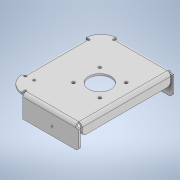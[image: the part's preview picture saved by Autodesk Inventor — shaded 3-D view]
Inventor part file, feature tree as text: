
AUTODESK INVENTOR PART (.ipt)
format: ipt  version: 2021 (Build 250183000, 183)  size: 284,160 bytes
history: native  units: mm
features: other x14, sketch x8, hole x4
ambient origin geometry x8: Origin, YZ Plane, XZ Plane, XY Plane, X Axis, Y Axis, Z Axis, Center Point
bodies: Body1 (feature_tree)
feature tree (26):
  other  "實體1"
  hole  "孔1"  [1 undecoded]
  other  "轉角外圓角2"
  other  "凸緣1"
  other  "凸緣2"
  other  "轉角外圓角1"
  hole  "孔4"  [1 undecoded]
  hole  "孔5"  [1 undecoded]
  hole  "孔6"  [1 undecoded]
  sketch  "草圖1"
  other  "平板1"
  sketch  "草圖2"
  sketch  "草圖3"
  sketch  "草圖4"
  other  "平板2"
  other  "折彎1"
  other  "轉角1"
  sketch  "草圖5"
  other  "平板3"
  other  "折彎2"
  other  "轉角2"
  sketch  "草圖8"
  sketch  "草圖9"
  sketch  "草圖10"
  other  "切割1"
  other  "定義1"
note: 4 required parameter values undecoded (feature->parameter linkage not recoverable at this tier; creation-order binding heuristic only, values carry confidence <= 0.55)
